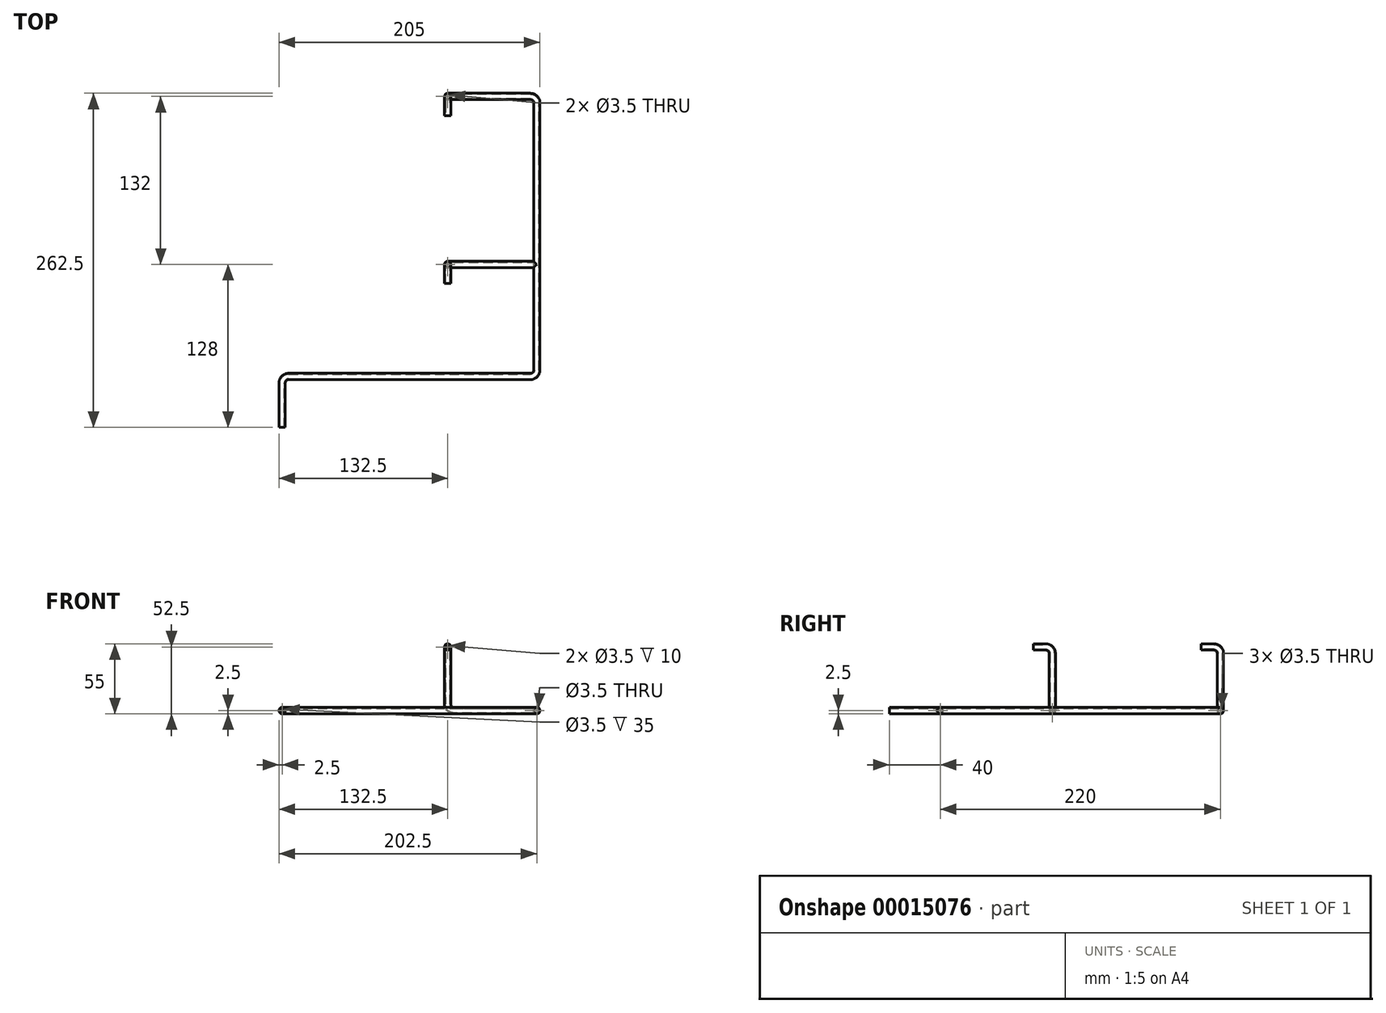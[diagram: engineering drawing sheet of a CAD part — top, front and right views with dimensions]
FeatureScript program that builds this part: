
annotation { "Feature Type Name" : "Feature", "Feature Type Description" : "" }
export const myFeature = defineFeature(function(context is Context, id is Id, definition is map)
    precondition{}
    {
        {
            var Q0;
            Q0=qCreatedBy(makeId("Top.planeOp"),FACE);
            var sketch = newSketch(context, id + "F0", { "sketchPlane" : qUnion([Q0])});
            skLineSegment(sketch, "E0.rect.top", {"start": v(95, 130) * mm, "end": v(30, 130) * mm});
            skLineSegment(sketch, "E0.rect.left", {"start": v(100, -85) * mm, "end": v(100, 125) * mm});
            skLineSegment(sketch, "E0.rect.right", {"start": v(-100, -130) * mm, "end": v(-100, -95) * mm});
            skPoint(sketch, "E0.rect.middle", {"position": v(0, 0) * mm});
            skLineSegment(sketch, "E1.0", {"start": v(95, -90) * mm, "end": v(-95, -90) * mm});
            skLineSegment(sketch, "E2.0", {"start": v(100, -2) * mm, "end": v(30, -2) * mm});
            skPoint(sketch, "E0.rect.bottom.start.orphan", {"position": v(100, -130) * mm});
            skPoint(sketch, "E3.orphan", {"position": v(-100, 130) * mm});
            skLineSegment(sketch, "E4", {"start": v(30, 130) * mm, "end": v(30, -2) * mm, "construction": true});
            skPoint(sketch, "E5.visualSharp", {"position": v(-100, -90) * mm});
            skArc(sketch, "E5.filletArc", {"start": v(-95, -90) * mm, "mid": v(-98.54, -91.46) * mm, "end": v(-100, -95) * mm});
            skPoint(sketch, "E6.visualSharp", {"position": v(100, -90) * mm});
            skArc(sketch, "E6.filletArc", {"start": v(95, -90) * mm, "mid": v(98.54, -88.54) * mm, "end": v(100, -85) * mm});
            skPoint(sketch, "E7.visualSharp", {"position": v(100, 130) * mm});
            skArc(sketch, "E7.filletArc", {"start": v(100, 125) * mm, "mid": v(98.54, 128.54) * mm, "end": v(95, 130) * mm});
            skSolve(sketch);
        }
        {
            var Q0;
            Q0=qCreatedBy(makeId("Front.planeOp"),FACE);
            var Q1;
            Q1=sQuery(id+"F0.wireOp",VERTEX,"E2.0.end");
            cPlane(context, id + "F1", {"entities" : qUnion([Q0, Q1]), "cplaneType" : CPlaneType.PLANE_POINT, "offset" : 150 * mm, "width" : 150 * mm, "height" : 150 * mm});
        }
        {
            var Q0;
            Q0=qCreatedBy(makeId("Front.planeOp"),FACE);
            var Q1;
            Q1=sQuery(id+"F0.wireOp",VERTEX,"E0.rect.top.end");
            cPlane(context, id + "F2", {"entities" : qUnion([Q0, Q1]), "cplaneType" : CPlaneType.PLANE_POINT, "offset" : 150 * mm, "width" : 150 * mm, "height" : 150 * mm});
        }
        {
            var Q0;
            Q0=qCreatedBy(id+"F2.planeOp",FACE);
            var sketch = newSketch(context, id + "F3", { "sketchPlane" : qUnion([Q0])});
            skLineSegment(sketch, "E8.0", {"start": v(95, 0) * mm, "end": v(35, 0) * mm});
            skLineSegment(sketch, "E9", {"start": v(30, 5) * mm, "end": v(30, 50) * mm});
            skPoint(sketch, "E10.visualSharp", {"position": v(30, 0) * mm});
            skArc(sketch, "E10.filletArc", {"start": v(30, 5) * mm, "mid": v(31.46, 1.46) * mm, "end": v(35, 0) * mm});
            skSolve(sketch);
        }
        {
            var Q0;
            Q0=qCreatedBy(id+"F1.planeOp",FACE);
            var sketch = newSketch(context, id + "F4", { "sketchPlane" : qUnion([Q0])});
            skLineSegment(sketch, "E11.0", {"start": v(95, 0) * mm, "end": v(35, 0) * mm});
            skArc(sketch, "E12.0", {"start": v(30, 5) * mm, "mid": v(31.46, 1.46) * mm, "end": v(35, 0) * mm});
            skLineSegment(sketch, "E13.0", {"start": v(30, 5) * mm, "end": v(30, 50) * mm});
            skSolve(sketch);
        }
        {
            var Q0;
            Q0=qCreatedBy(makeId("Right.planeOp"),FACE);
            var Q1;
            Q1=sQuery(id+"F4.wireOp",VERTEX,"E13.0.end");
            cPlane(context, id + "F5", {"entities" : qUnion([Q0, Q1]), "cplaneType" : CPlaneType.PLANE_POINT, "offset" : 150 * mm, "width" : 150 * mm, "height" : 150 * mm});
        }
        {
            var Q0;
            Q0=qCreatedBy(id+"F5.planeOp",FACE);
            var sketch = newSketch(context, id + "F6", { "sketchPlane" : qUnion([Q0])});
            skLineSegment(sketch, "E14.0", {"start": v(-2, 5) * mm, "end": v(-2, 45) * mm});
            skLineSegment(sketch, "E15.0", {"start": v(130, 5) * mm, "end": v(130, 45) * mm});
            skLineSegment(sketch, "E16", {"start": v(-7, 50) * mm, "end": v(-17, 50) * mm});
            skLineSegment(sketch, "E17", {"start": v(125, 50) * mm, "end": v(115, 50) * mm});
            skPoint(sketch, "E18.visualSharp", {"position": v(-2, 50) * mm});
            skArc(sketch, "E18.filletArc", {"start": v(-2, 45) * mm, "mid": v(-3.46, 48.54) * mm, "end": v(-7, 50) * mm});
            skPoint(sketch, "E19.visualSharp", {"position": v(130, 50) * mm});
            skArc(sketch, "E19.filletArc", {"start": v(130, 45) * mm, "mid": v(128.54, 48.54) * mm, "end": v(125, 50) * mm});
            skSolve(sketch);
        }
        {
            var Q0;
            Q0=qCreatedBy(makeId("Front.planeOp"),FACE);
            var Q1;
            Q1=sQuery(id+"F0.wireOp",VERTEX,"E0.rect.right.start");
            cPlane(context, id + "F7", {"entities" : qUnion([Q0, Q1]), "cplaneType" : CPlaneType.PLANE_POINT, "offset" : 150 * mm, "width" : 150 * mm, "height" : 150 * mm});
        }
        {
            var Q0;
            Q0=qCreatedBy(id+"F7.planeOp",FACE);
            var sketch = newSketch(context, id + "F8", { "sketchPlane" : qUnion([Q0])});
            skPoint(sketch, "E20.0", {"position": v(-100, 0) * mm});
            skCircle(sketch, "E21", {"center": v(-100, 0) * mm, "radius": 1.75 * mm});
            skCircle(sketch, "E22", {"center": v(-100, 0) * mm, "radius": 2.5 * mm});
            skSolve(sketch);
        }
        {
            var Q0;
            Q0=makeQuery(id+"F8.imprint","IMPRINT",FACE,{"disambiguationData":[TD([[makeQuery(id+"F8.imprint","IMPRINT",EDGE,{"derivedFrom":sQuery(id+"F8.wireOp",EDGE,"E21")}),-1.0]])]});
            var Q1;
            Q1=sQuery(id+"F0.wireOp",EDGE,"E0.rect.right");
            var Q2;
            Q2=sQuery(id+"F0.wireOp",EDGE,"E5.filletArc");
            var Q3;
            Q3=sQuery(id+"F0.wireOp",EDGE,"E1.0");
            var Q4;
            Q4=sQuery(id+"F0.wireOp",EDGE,"E6.filletArc");
            var Q5;
            Q5=sQuery(id+"F0.wireOp",EDGE,"E0.rect.left");
            var Q6;
            Q6=sQuery(id+"F0.wireOp",EDGE,"E7.filletArc");
            var Q7;
            Q7=sQuery(id+"F3.wireOp",EDGE,"E10.filletArc");
            var Q8;
            Q8=sQuery(id+"F6.wireOp",EDGE,"E15.0");
            var Q9;
            Q9=sQuery(id+"F6.wireOp",EDGE,"E19.filletArc");
            var Q10;
            Q10=sQuery(id+"F6.wireOp",EDGE,"E17");
            var Q11;
            Q11=sQuery(id+"F3.wireOp",EDGE,"E8.0");
            sweep(context, id + "F9", {"profiles" : qUnion([Q0]), "path" : qUnion([Q1, Q2, Q3, Q4, Q5, Q6, Q7, Q8, Q9, Q10, Q11])});
        }
        {
            var Q0;
            Q0=qCreatedBy(makeId("Front.planeOp"),FACE);
            var Q1;
            Q1=sQuery(id+"F6.wireOp",VERTEX,"E16.end");
            cPlane(context, id + "F10", {"entities" : qUnion([Q0, Q1]), "cplaneType" : CPlaneType.PLANE_POINT, "offset" : 150 * mm, "width" : 150 * mm, "height" : 150 * mm});
        }
        {
            var Q0;
            Q0=qCreatedBy(id+"F10.planeOp",FACE);
            var sketch = newSketch(context, id + "F11", { "sketchPlane" : qUnion([Q0])});
            skPoint(sketch, "E23.0", {"position": v(30, 50) * mm});
            skCircle(sketch, "E24", {"center": v(30, 50) * mm, "radius": 1.75 * mm});
            skCircle(sketch, "E25", {"center": v(30, 50) * mm, "radius": 2.5 * mm});
            skSolve(sketch);
        }
        {
            var Q0;
            Q0=makeQuery(id+"F11.imprint","IMPRINT",FACE,{"disambiguationData":[TD([[makeQuery(id+"F11.imprint","IMPRINT",EDGE,{"derivedFrom":sQuery(id+"F11.wireOp",EDGE,"E24")}),-1.0]])]});
            var Q1;
            Q1=sQuery(id+"F6.wireOp",EDGE,"E16");
            var Q2;
            Q2=sQuery(id+"F6.wireOp",EDGE,"E18.filletArc");
            var Q3;
            Q3=sQuery(id+"F6.wireOp",EDGE,"E14.0");
            var Q4;
            Q4=sQuery(id+"F4.wireOp",EDGE,"E12.0");
            var Q5;
            Q5=sQuery(id+"F4.wireOp",EDGE,"E11.0");
            sweep(context, id + "F12", {"operationType" : NewBodyOperationType.ADD, "profiles" : qUnion([Q0]), "path" : qUnion([Q1, Q2, Q3, Q4, Q5])});
        }
        {
            var Q0;
            Q0=makeQuery(id+"F12.opSweep","CAP_FACE",FACE,{"disambiguationData":[OSD([sQuery(id+"F4.wireOp",VERTEX,"E11.0.start"),sQuery(id+"F11.wireOp",EDGE,"E24"),sQuery(id+"F11.wireOp",EDGE,"E25")])],"isStart":false});
            var Q1;
            Q1=makeQuery(id+"F9.opSweep","SWEPT_FACE",FACE,{"disambiguationData":[OSD([sQuery(id+"F0.wireOp",EDGE,"E0.rect.left"),sQuery(id+"F8.wireOp",EDGE,"E22")])]});
            extrude(context, id + "F13", {"entities" : qUnion([Q0]), "operationType" : NewBodyOperationType.ADD, "endBound" : BoundingType.UP_TO_BODY, "endBoundEntityBody" : qUnion([Q1]), "depth" : 25 * mm});
        }
    });
